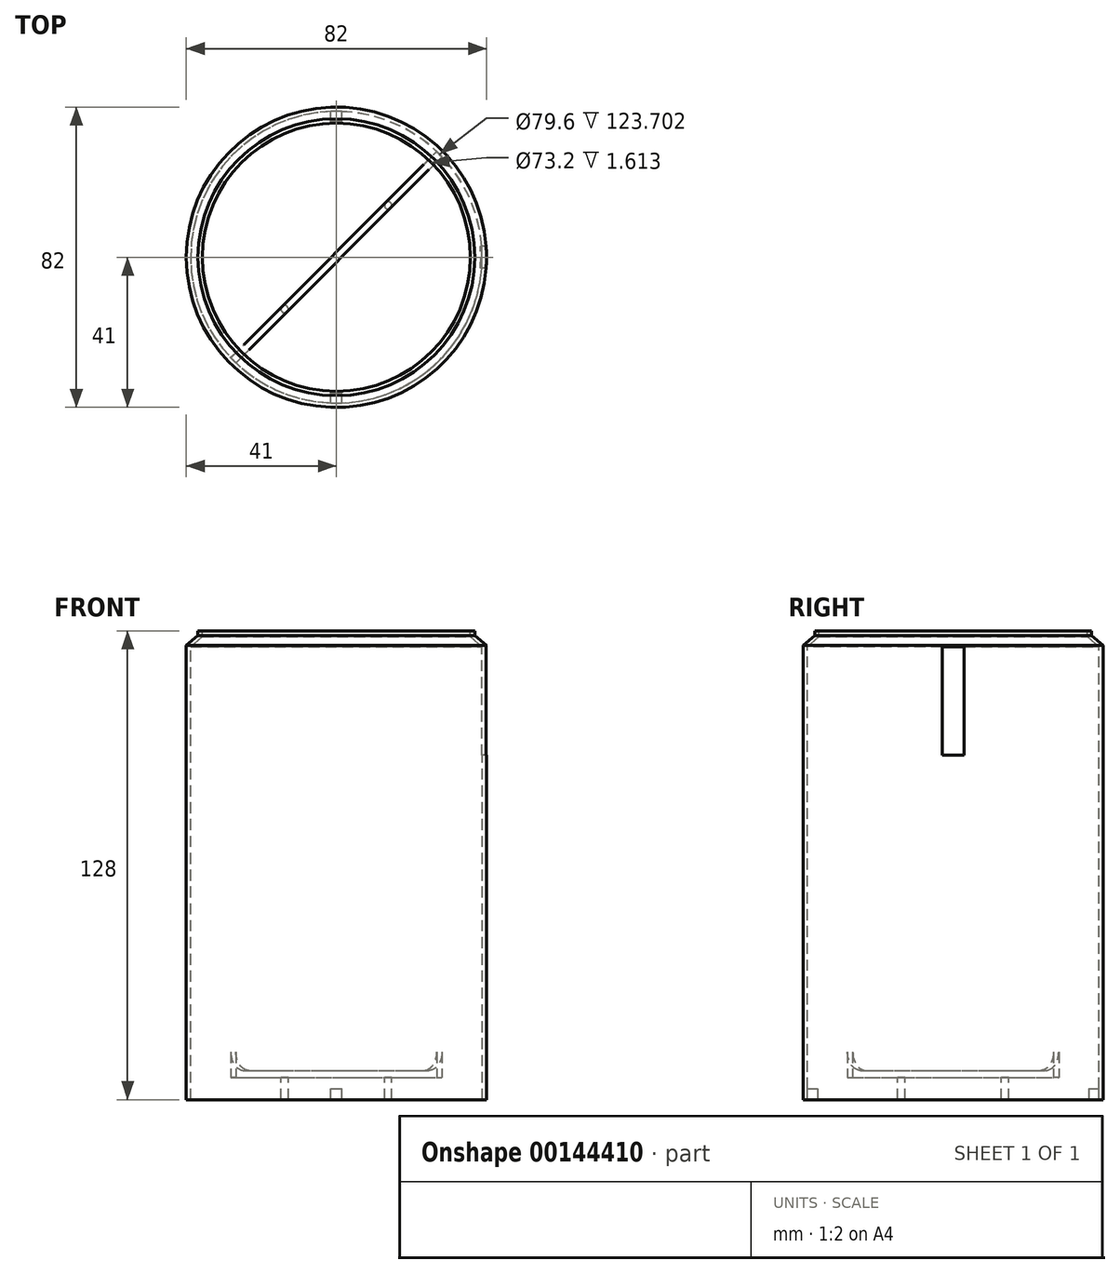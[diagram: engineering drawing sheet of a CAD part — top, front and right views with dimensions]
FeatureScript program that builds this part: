
annotation { "Feature Type Name" : "Feature", "Feature Type Description" : "" }
export const myFeature = defineFeature(function(context is Context, id is Id, definition is map)
    precondition{}
    {
        {
            var Q0;
            Q0=qCreatedBy(makeId("Right.planeOp"),FACE);
            var sketch = newSketch(context, id + "F0", { "sketchPlane" : qUnion([Q0])});
            skLineSegment(sketch, "E0", {"start": v(-41, 0) * mm, "end": v(-41, 124) * mm});
            skLineSegment(sketch, "E1", {"start": v(-39.8, 123.7) * mm, "end": v(-39.8, 0) * mm});
            skLineSegment(sketch, "E2", {"start": v(-39.8, 0) * mm, "end": v(-41, 0) * mm});
            skLineSegment(sketch, "E3", {"start": v(0, 64.87) * mm, "end": v(0, 0) * mm, "construction": true});
            skLineSegment(sketch, "E4", {"start": v(-37.8, 128) * mm, "end": v(-36.6, 128) * mm});
            skLineSegment(sketch, "E5", {"start": v(-37.8, 128) * mm, "end": v(-37.8, 126.69) * mm});
            skLineSegment(sketch, "E6", {"start": v(-36.6, 128) * mm, "end": v(-36.6, 126.39) * mm});
            skLineSegment(sketch, "E7", {"start": v(-37.8, 126.69) * mm, "end": v(-41, 124) * mm});
            skLineSegment(sketch, "E8", {"start": v(-36.6, 126.39) * mm, "end": v(-39.8, 123.7) * mm});
            skSolve(sketch);
        }
        {
            var Q0;
            Q0 = qSketchRegion(id + "F0", true);
            var Q1;
            Q1=sQuery(id+"F0.wireOp",EDGE,"E3");
            revolve(context, id + "F1", {"entities" : qUnion([Q0]), "axis" : qUnion([Q1]), "revolveType" : RevolveType.FULL});
        }
        {
            var Q0;
            Q0=qCreatedBy(makeId("Right.planeOp"),FACE);
            var sketch = newSketch(context, id + "F2", { "sketchPlane" : qUnion([Q0])});
            skLineSegment(sketch, "E9.bottom", {"start": v(-3, 124) * mm, "end": v(3, 124) * mm});
            skLineSegment(sketch, "E9.top", {"start": v(-3, 94) * mm, "end": v(3, 94) * mm});
            skLineSegment(sketch, "E9.left", {"start": v(-3, 124) * mm, "end": v(-3, 94) * mm});
            skLineSegment(sketch, "E9.right", {"start": v(3, 124) * mm, "end": v(3, 94) * mm});
            skSolve(sketch);
        }
        {
            var Q0;
            Q0 = qSketchRegion(id + "F2", true);
            extrude(context, id + "F3", {"entities" : qUnion([Q0]), "operationType" : NewBodyOperationType.REMOVE, "endBound" : BoundingType.THROUGH_ALL, "depth" : 25 * mm});
        }
        {
            var Q0;
            Q0=makeQuery(id+"F1.opRevolve","SWEPT_FACE",FACE,{"disambiguationData":[OSD([sQuery(id+"F0.wireOp",EDGE,"E2")])]});
            var sketch = newSketch(context, id + "F4", { "sketchPlane" : qUnion([Q0])});
            skLineSegment(sketch, "E10.bottom", {"start": v(-1.5, 40.97) * mm, "end": v(1.5, 40.97) * mm});
            skLineSegment(sketch, "E10.top", {"start": v(-1.5, -40.97) * mm, "end": v(1.5, -40.97) * mm});
            skLineSegment(sketch, "E10.left", {"start": v(-1.5, 40.97) * mm, "end": v(-1.5, -40.97) * mm});
            skLineSegment(sketch, "E10.right", {"start": v(1.5, 40.97) * mm, "end": v(1.5, -40.97) * mm});
            skSolve(sketch);
        }
        {
            var Q0;
            Q0 = qSketchRegion(id + "F4", true);
            extrude(context, id + "F5", {"entities" : qUnion([Q0]), "operationType" : NewBodyOperationType.ADD, "oppositeDirection" : true, "depth" : 3 * mm});
        }
        {
            var Q0;
            {var subQ0=sQuery(id+"F4.wireOp",EDGE,"E10.right");var subQ1=sQuery(id+"F4.wireOp",EDGE,"E10.left");var subQ2=sQuery(id+"F4.wireOp",EDGE,"E10.top");var subQ3=sQuery(id+"F4.wireOp",EDGE,"E10.bottom");Q0=makeQuery(id+"Fm3hgB5jgAHXXEo_1.1.F5.boolean.opBoolean","MERGE",FACE,{"derivedFrom":[makeQuery(id+"F5.boolean.opBoolean","MERGE",FACE,{"derivedFrom":[makeQuery(id+"F1.opRevolve","SWEPT_FACE",FACE,{"disambiguationData":[OSD([sQuery(id+"F0.wireOp",EDGE,"E2")])]}),makeQuery(id+"F5.opExtrude","CAP_FACE",FACE,{"disambiguationData":[OSD([subQ3,subQ2,subQ1,subQ0])],"isStart":true})]}),makeQuery(id+"Fm3hgB5jgAHXXEo_1.1.F5.opExtrude","CAP_FACE",FACE,{"disambiguationData":[OSD([subQ3,subQ2,subQ1,subQ0])],"isStart":true})]});}
            var sketch = newSketch(context, id + "F6", { "sketchPlane" : qUnion([Q0])});
            skCircle(sketch, "E11", {"center": v(0, 0) * mm, "radius": 37 * mm});
            skSolve(sketch);
        }
        {
            var Q0;
            Q0 = qSketchRegion(id + "F6", true);
            extrude(context, id + "F7", {"entities" : qUnion([Q0]), "operationType" : NewBodyOperationType.REMOVE, "oppositeDirection" : true, "depth" : 5 * mm});
        }
        {
            var Q0;
            {var subQ0=sQuery(id+"F4.wireOp",EDGE,"E10.right");var subQ1=sQuery(id+"F4.wireOp",EDGE,"E10.left");var subQ2=sQuery(id+"F4.wireOp",EDGE,"E10.top");var subQ3=sQuery(id+"F4.wireOp",EDGE,"E10.bottom");Q0=makeQuery(id+"Fm3hgB5jgAHXXEo_1.1.F5.boolean.opBoolean","MERGE",FACE,{"derivedFrom":[makeQuery(id+"F5.boolean.opBoolean","MERGE",FACE,{"derivedFrom":[makeQuery(id+"F1.opRevolve","SWEPT_FACE",FACE,{"disambiguationData":[OSD([sQuery(id+"F0.wireOp",EDGE,"E2")])]}),makeQuery(id+"F5.opExtrude","CAP_FACE",FACE,{"disambiguationData":[OSD([subQ3,subQ2,subQ1,subQ0])],"isStart":true})]}),makeQuery(id+"Fm3hgB5jgAHXXEo_1.1.F5.opExtrude","CAP_FACE",FACE,{"disambiguationData":[OSD([subQ3,subQ2,subQ1,subQ0])],"isStart":true})]});}
            cPlane(context, id + "F8", {"entities" : qUnion([Q0]), "cplaneType" : CPlaneType.OFFSET, "offset" : 6 * mm, "oppositeDirection" : true, "width" : 150 * mm, "height" : 150 * mm});
        }
        {
            var Q0;
            Q0=qCreatedBy(id+"F8.planeOp",FACE);
            var sketch = newSketch(context, id + "F9", { "sketchPlane" : qUnion([Q0])});
            skLineSegment(sketch, "E12", {"start": v(-28.84, 27.43) * mm, "end": v(27.43, -28.84) * mm});
            skLineSegment(sketch, "E13", {"start": v(-27.43, 28.84) * mm, "end": v(28.84, -27.43) * mm});
            skLineSegment(sketch, "E14", {"start": v(-27.43, 27.43) * mm, "end": v(0, 0) * mm, "construction": true});
            skArc(sketch, "E15", {"start": v(-27.43, 28.84) * mm, "mid": v(-28.34, 28.34) * mm, "end": v(-28.84, 27.43) * mm});
            skArc(sketch, "E16", {"start": v(27.43, -28.84) * mm, "mid": v(28.27, -28.27) * mm, "end": v(28.84, -27.43) * mm});
            skSolve(sketch);
        }
        {
            var Q0;
            Q0 = qSketchRegion(id + "F9", true);
            extrude(context, id + "F10", {"entities" : qUnion([Q0]), "operationType" : NewBodyOperationType.ADD, "oppositeDirection" : true, "depth" : 2 * mm});
        }
        {
            var Q0;
            Q0=makeQuery(id+"F10.opExtrude","CAP_FACE",FACE,{"disambiguationData":[OSD([sQuery(id+"F9.wireOp",EDGE,"E12"),sQuery(id+"F9.wireOp",EDGE,"E13"),sQuery(id+"F9.wireOp",EDGE,"E15"),sQuery(id+"F9.wireOp",EDGE,"E16")])],"isStart":true});
            var sketch = newSketch(context, id + "F11", { "sketchPlane" : qUnion([Q0])});
            skLineSegment(sketch, "E17", {"start": v(0, 0) * mm, "end": v(11.82, 11.82) * mm, "construction": true});
            skLineSegment(sketch, "E18", {"start": v(-14.14, 14.14) * mm, "end": v(0, 0) * mm, "construction": true});
            skCircle(sketch, "E19", {"center": v(-14.14, 14.14) * mm, "radius": 1 * mm});
            skCircle(sketch, "E20.MirrorC", {"center": v(14.14, -14.14) * mm, "radius": 1 * mm});
            skSolve(sketch);
        }
        {
            var Q0;
            Q0 = qSketchRegion(id + "F11", true);
            var Q1;
            {var subQ0=sQuery(id+"F4.wireOp",EDGE,"E10.right");var subQ1=sQuery(id+"F4.wireOp",EDGE,"E10.left");var subQ2=sQuery(id+"F4.wireOp",EDGE,"E10.top");var subQ3=sQuery(id+"F4.wireOp",EDGE,"E10.bottom");Q1=makeQuery(id+"Fm3hgB5jgAHXXEo_1.1.F5.boolean.opBoolean","MERGE",FACE,{"derivedFrom":[makeQuery(id+"F5.boolean.opBoolean","MERGE",FACE,{"derivedFrom":[makeQuery(id+"F1.opRevolve","SWEPT_FACE",FACE,{"disambiguationData":[OSD([sQuery(id+"F0.wireOp",EDGE,"E2")])]}),makeQuery(id+"F5.opExtrude","CAP_FACE",FACE,{"disambiguationData":[OSD([subQ3,subQ2,subQ1,subQ0])],"isStart":true})]}),makeQuery(id+"Fm3hgB5jgAHXXEo_1.1.F5.opExtrude","CAP_FACE",FACE,{"disambiguationData":[OSD([subQ3,subQ2,subQ1,subQ0])],"isStart":true})]});}
            extrude(context, id + "F12", {"entities" : qUnion([Q0]), "operationType" : NewBodyOperationType.ADD, "endBound" : BoundingType.UP_TO_SURFACE, "endBoundEntityFace" : qUnion([Q1]), "depth" : 25 * mm});
        }
        {
            var Q0;
            Q0=makeQuery(id+"F10.boolean.opBoolean","INTERSECT",EDGE,{"disambiguationData":[OD(1.0)],"derivedFrom":[makeQuery(id+"F1.opRevolve","SWEPT_FACE",FACE,{"disambiguationData":[OSD([sQuery(id+"F0.wireOp",EDGE,"E1")])]}),makeQuery(id+"F10.opExtrude","CAP_FACE",FACE,{"disambiguationData":[OSD([sQuery(id+"F9.wireOp",EDGE,"E12"),sQuery(id+"F9.wireOp",EDGE,"E13"),sQuery(id+"F9.wireOp",EDGE,"E15"),sQuery(id+"F9.wireOp",EDGE,"E16")])],"isStart":false})]});
            var Q1;
            Q1=makeQuery(id+"FqhN9CS0vOLvWld_1.1.F10.boolean.opBoolean","INTERSECT",EDGE,{"disambiguationData":[OD(1.0)],"derivedFrom":[makeQuery(id+"F1.opRevolve","SWEPT_FACE",FACE,{"disambiguationData":[OSD([sQuery(id+"F0.wireOp",EDGE,"E1")])]}),makeQuery(id+"FqhN9CS0vOLvWld_1.1.F10.opExtrude","CAP_FACE",FACE,{"disambiguationData":[OSD([sQuery(id+"F9.wireOp",EDGE,"E12"),sQuery(id+"F9.wireOp",EDGE,"E13"),sQuery(id+"F9.wireOp",EDGE,"E15"),sQuery(id+"F9.wireOp",EDGE,"E16")])],"isStart":false})]});
            var Q2;
            Q2=makeQuery(id+"F10.boolean.opBoolean","INTERSECT",EDGE,{"disambiguationData":[OD(0.0)],"derivedFrom":[makeQuery(id+"F1.opRevolve","SWEPT_FACE",FACE,{"disambiguationData":[OSD([sQuery(id+"F0.wireOp",EDGE,"E1")])]}),makeQuery(id+"F10.opExtrude","CAP_FACE",FACE,{"disambiguationData":[OSD([sQuery(id+"F9.wireOp",EDGE,"E12"),sQuery(id+"F9.wireOp",EDGE,"E13"),sQuery(id+"F9.wireOp",EDGE,"E15"),sQuery(id+"F9.wireOp",EDGE,"E16")])],"isStart":false})]});
            var Q3;
            Q3=makeQuery(id+"FqhN9CS0vOLvWld_1.1.F10.boolean.opBoolean","INTERSECT",EDGE,{"disambiguationData":[OD(0.0)],"derivedFrom":[makeQuery(id+"F1.opRevolve","SWEPT_FACE",FACE,{"disambiguationData":[OSD([sQuery(id+"F0.wireOp",EDGE,"E1")])]}),makeQuery(id+"FqhN9CS0vOLvWld_1.1.F10.opExtrude","CAP_FACE",FACE,{"disambiguationData":[OSD([sQuery(id+"F9.wireOp",EDGE,"E12"),sQuery(id+"F9.wireOp",EDGE,"E13"),sQuery(id+"F9.wireOp",EDGE,"E15"),sQuery(id+"F9.wireOp",EDGE,"E16")])],"isStart":false})]});
            fillet(context, id + "F13", {"entities" : qUnion([Q0, Q1, Q2, Q3]), "radius" : 5 * mm, "tangentPropagation" : true, "allowEdgeOverflow" : false});
        }
    });
